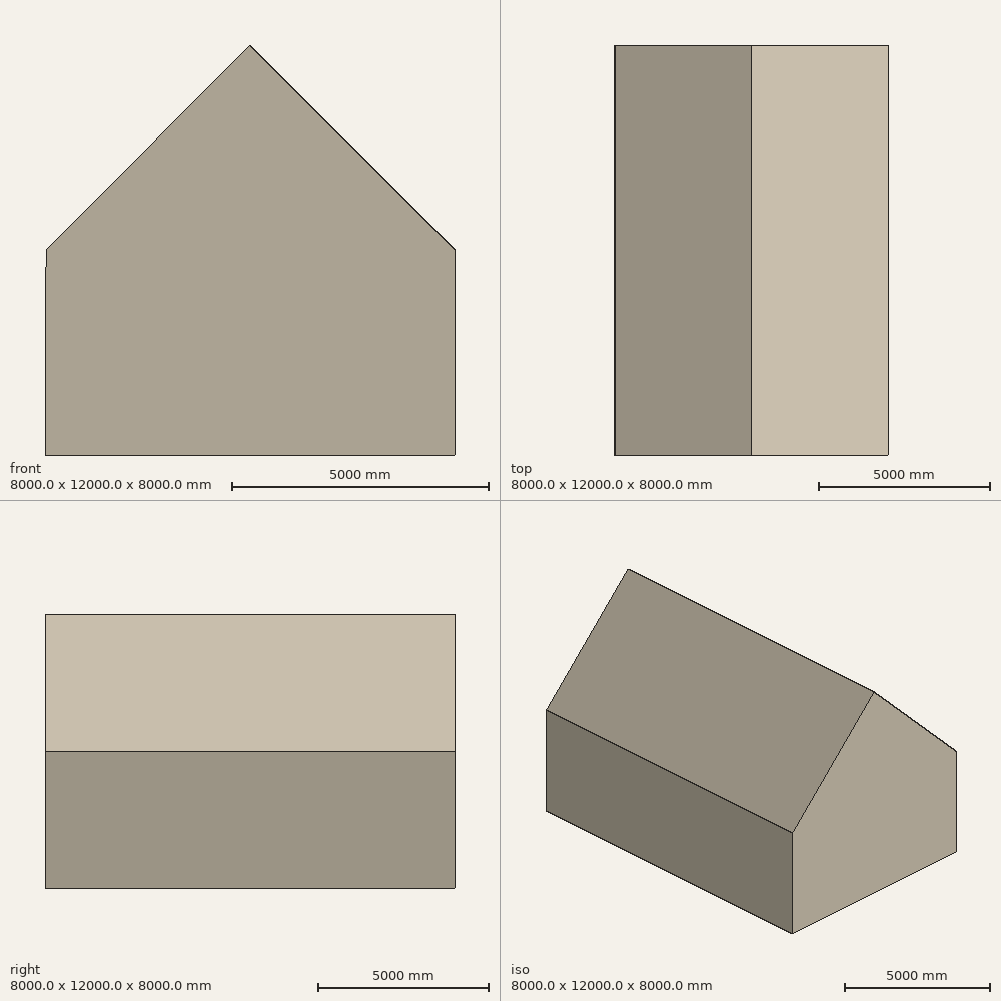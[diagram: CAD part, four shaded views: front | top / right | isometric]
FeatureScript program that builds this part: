
annotation { "Feature Type Name" : "Feature", "Feature Type Description" : "" }
export const myFeature = defineFeature(function(context is Context, id is Id, definition is map)
    precondition{}
    {
        {
            var Q0;
            Q0=qCreatedBy(makeId("Front.planeOp"),FACE);
            var sketch = newSketch(context, id + "F0", { "sketchPlane" : qUnion([Q0])});
            skLineSegment(sketch, "E0", {"start": v(-3991.67, 540) * mm, "end": v(4008.33, 540) * mm});
            skLineSegment(sketch, "E1", {"start": v(4008.33, 540) * mm, "end": v(4008.33, 4540) * mm});
            skLineSegment(sketch, "E2", {"start": v(4008.33, 4540) * mm, "end": v(0, 8540) * mm});
            skLineSegment(sketch, "E3", {"start": v(0, 8540) * mm, "end": v(-3980.18, 4540) * mm});
            skLineSegment(sketch, "E4", {"start": v(-3980.18, 4540) * mm, "end": v(-3991.67, 540) * mm});
            skLineSegment(sketch, "E5", {"start": v(-3980.18, 4540) * mm, "end": v(4008.33, 4540) * mm});
            skSolve(sketch);
        }
        {
            var Q0;
            Q0=makeQuery(id+"F0.imprint","IMPRINT",FACE,{"disambiguationData":[TD([[makeQuery(id+"F0.imprint","IMPRINT",EDGE,{"derivedFrom":sQuery(id+"F0.wireOp",EDGE,"E2")}),1.0]])]});
            var Q1;
            Q1=makeQuery(id+"F0.imprint","IMPRINT",FACE,{"disambiguationData":[TD([[makeQuery(id+"F0.imprint","IMPRINT",EDGE,{"derivedFrom":sQuery(id+"F0.wireOp",EDGE,"E0")}),1.0]])]});
            extrude(context, id + "F1", {"entities" : qUnion([Q0, Q1]), "depth" : 12000 * mm});
        }
    });
